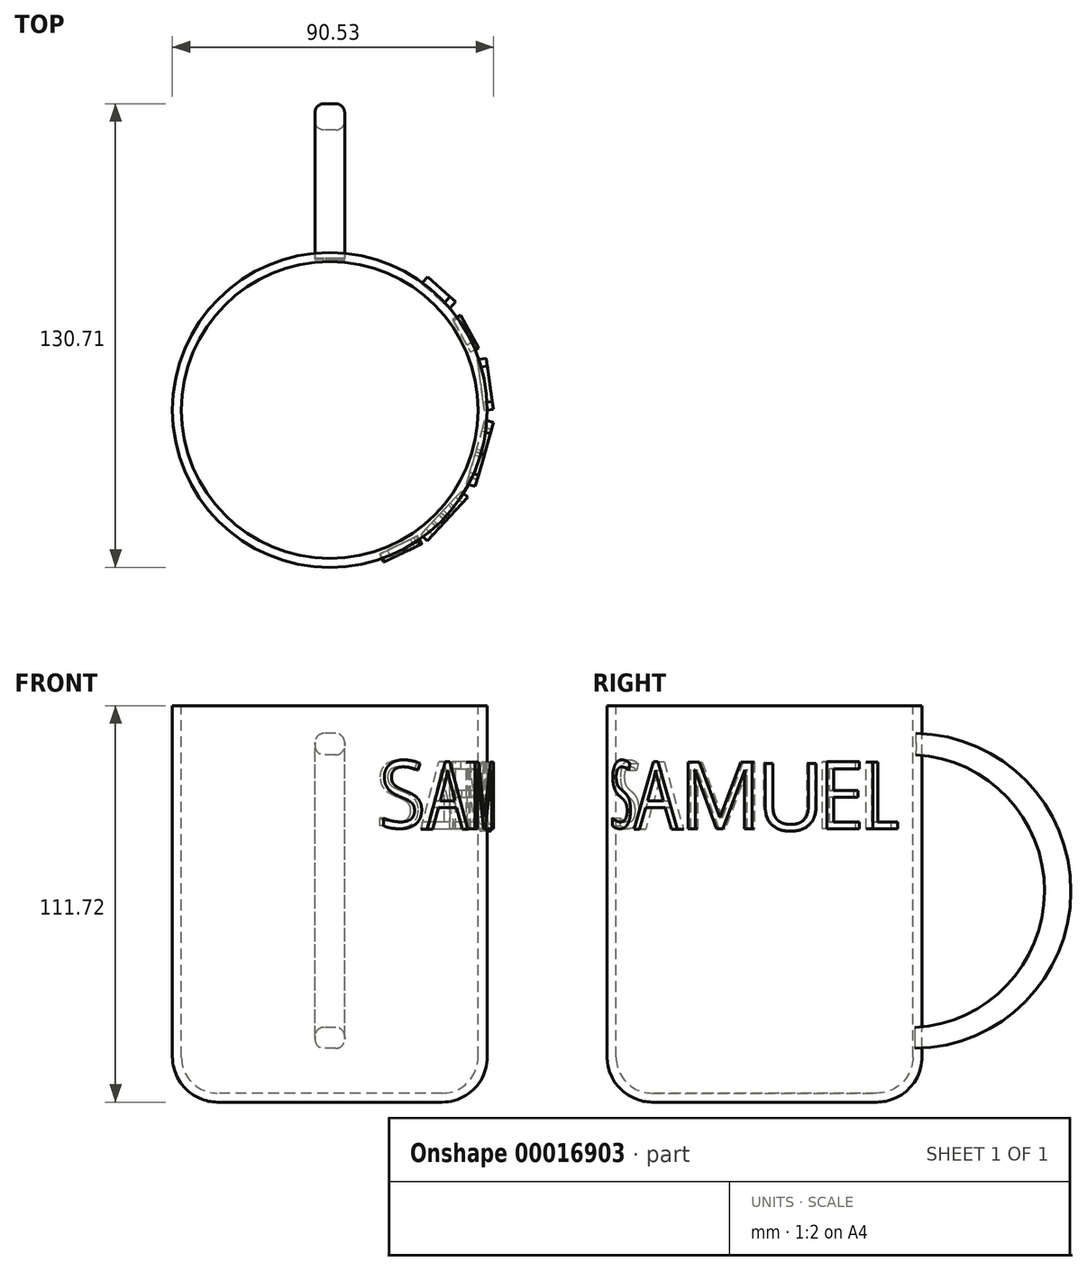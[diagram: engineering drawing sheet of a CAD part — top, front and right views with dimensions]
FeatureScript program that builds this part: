
annotation { "Feature Type Name" : "Feature", "Feature Type Description" : "" }
export const myFeature = defineFeature(function(context is Context, id is Id, definition is map)
    precondition{}
    {
        {
            var Q0;
            Q0=qCreatedBy(makeId("Front.planeOp"),FACE);
            var sketch = newSketch(context, id + "F0", { "sketchPlane" : qUnion([Q0])});
            skLineSegment(sketch, "E0.bottom", {"start": v(0, 46.6) * mm, "end": v(44.36, 46.6) * mm});
            skLineSegment(sketch, "E0.top", {"start": v(0, -65.12) * mm, "end": v(44.36, -65.12) * mm});
            skLineSegment(sketch, "E0.left", {"start": v(0, 46.6) * mm, "end": v(0, -65.12) * mm});
            skLineSegment(sketch, "E0.right", {"start": v(44.36, 46.6) * mm, "end": v(44.36, -65.12) * mm});
            skSolve(sketch);
        }
        {
            var Q0;
            Q0=makeQuery(id+"F0.imprint","IMPRINT",FACE,{"disambiguationData":[TD([[makeQuery(id+"F0.imprint","IMPRINT",EDGE,{"derivedFrom":sQuery(id+"F0.wireOp",EDGE,"E0.bottom")}),-1.0]])]});
            var Q1;
            Q1=sQuery(id+"F0.wireOp",EDGE,"E0.left");
            revolve(context, id + "F1", {"entities" : qUnion([Q0]), "axis" : qUnion([Q1]), "revolveType" : RevolveType.FULL});
        }
        {
            var Q0;
            Q0=makeQuery(id+"F1.opRevolve","SWEPT_EDGE",EDGE,{"disambiguationData":[OSD([sQuery(id+"F0.wireOp",EDGE,"E0.top"),sQuery(id+"F0.wireOp",EDGE,"E0.right")])]});
            fillet(context, id + "F2", {"entities" : qUnion([Q0]), "radius" : 12.7 * mm, "tangentPropagation" : true, "allowEdgeOverflow" : false});
        }
        {
            var Q0;
            Q0=makeQuery(id+"F1.opRevolve","SWEPT_FACE",FACE,{"disambiguationData":[OSD([sQuery(id+"F0.wireOp",EDGE,"E0.bottom")])]});
            shell(context, id + "F3", {"entities" : qUnion([Q0]), "thickness" : 2.54 * mm});
        }
        {
            var Q0;
            Q0=qCreatedBy(makeId("Right.planeOp"),FACE);
            var sketch = newSketch(context, id + "F4", { "sketchPlane" : qUnion([Q0])});
            skText(sketch, "E1", { "text": "S", "fontName": "OpenSans-Regular.ttf"});
            const initialGuessF4  = {"E1": [-0.0061, 0.0296, 1, 0, 0.01905]};
            skSetInitialGuess(sketch, initialGuessF4);
            skSolve(sketch);
        }
        {
            var Q0;
            Q0=makeQuery(id+"F4.imprint","IMPRINT",FACE,{"disambiguationData":[TD([[makeQuery(id+"F4.imprint","IMPRINT",EDGE,{"derivedFrom":sQuery(id+"F4.wireOp",EDGE,"E1.sketch_text.stroke-0")}),-1.0]])]});
            extrude(context, id + "F5", {"entities" : qUnion([Q0]), "depth" : 2.54 * mm});
        }
        {
            var Q0;
            Q0=makeQuery(id+"F5.opExtrude","SWEPT_BODY",BODY,{"disambiguationData":[OSD([sQuery(id+"F4.wireOp",EDGE,"E1.sketch_text.stroke-0"),sQuery(id+"F4.wireOp",EDGE,"E1.sketch_text.stroke-1"),sQuery(id+"F4.wireOp",EDGE,"E1.sketch_text.stroke-2"),sQuery(id+"F4.wireOp",EDGE,"E1.sketch_text.stroke-3"),sQuery(id+"F4.wireOp",EDGE,"E1.sketch_text.stroke-4"),sQuery(id+"F4.wireOp",EDGE,"E1.sketch_text.stroke-5"),sQuery(id+"F4.wireOp",EDGE,"E1.sketch_text.stroke-6"),sQuery(id+"F4.wireOp",EDGE,"E1.sketch_text.stroke-7"),sQuery(id+"F4.wireOp",EDGE,"E1.sketch_text.stroke-8"),sQuery(id+"F4.wireOp",EDGE,"E1.sketch_text.stroke-9"),sQuery(id+"F4.wireOp",EDGE,"E1.sketch_text.stroke-10"),sQuery(id+"F4.wireOp",EDGE,"E1.sketch_text.stroke-11"),sQuery(id+"F4.wireOp",EDGE,"E1.sketch_text.stroke-12"),sQuery(id+"F4.wireOp",EDGE,"E1.sketch_text.stroke-13"),sQuery(id+"F4.wireOp",EDGE,"E1.sketch_text.stroke-14"),sQuery(id+"F4.wireOp",EDGE,"E1.sketch_text.stroke-15"),sQuery(id+"F4.wireOp",EDGE,"E1.sketch_text.stroke-16"),sQuery(id+"F4.wireOp",EDGE,"E1.sketch_text.stroke-17"),sQuery(id+"F4.wireOp",EDGE,"E1.sketch_text.stroke-18"),sQuery(id+"F4.wireOp",EDGE,"E1.sketch_text.stroke-19"),sQuery(id+"F4.wireOp",EDGE,"E1.sketch_text.stroke-20"),sQuery(id+"F4.wireOp",EDGE,"E1.sketch_text.stroke-21"),sQuery(id+"F4.wireOp",EDGE,"E1.sketch_text.stroke-22"),sQuery(id+"F4.wireOp",EDGE,"E1.sketch_text.stroke-23"),sQuery(id+"F4.wireOp",EDGE,"E1.sketch_text.stroke-24")])]});
            transform(context, id + "F6", {"entities" : qUnion([Q0]), "transformType" : TransformType.TRANSLATION_3D, "dx" : 42.69 * mm, "dy" : 0 * mm, "dz" : -17.4 * mm, "makeCopy" : false});
        }
        {
            var Q0;
            Q0=makeQuery(id+"F5.opExtrude","SWEPT_BODY",BODY,{"disambiguationData":[OSD([sQuery(id+"F4.wireOp",EDGE,"E1.sketch_text.stroke-0"),sQuery(id+"F4.wireOp",EDGE,"E1.sketch_text.stroke-1"),sQuery(id+"F4.wireOp",EDGE,"E1.sketch_text.stroke-2"),sQuery(id+"F4.wireOp",EDGE,"E1.sketch_text.stroke-3"),sQuery(id+"F4.wireOp",EDGE,"E1.sketch_text.stroke-4"),sQuery(id+"F4.wireOp",EDGE,"E1.sketch_text.stroke-5"),sQuery(id+"F4.wireOp",EDGE,"E1.sketch_text.stroke-6"),sQuery(id+"F4.wireOp",EDGE,"E1.sketch_text.stroke-7"),sQuery(id+"F4.wireOp",EDGE,"E1.sketch_text.stroke-8"),sQuery(id+"F4.wireOp",EDGE,"E1.sketch_text.stroke-9"),sQuery(id+"F4.wireOp",EDGE,"E1.sketch_text.stroke-10"),sQuery(id+"F4.wireOp",EDGE,"E1.sketch_text.stroke-11"),sQuery(id+"F4.wireOp",EDGE,"E1.sketch_text.stroke-12"),sQuery(id+"F4.wireOp",EDGE,"E1.sketch_text.stroke-13"),sQuery(id+"F4.wireOp",EDGE,"E1.sketch_text.stroke-14"),sQuery(id+"F4.wireOp",EDGE,"E1.sketch_text.stroke-15"),sQuery(id+"F4.wireOp",EDGE,"E1.sketch_text.stroke-16"),sQuery(id+"F4.wireOp",EDGE,"E1.sketch_text.stroke-17"),sQuery(id+"F4.wireOp",EDGE,"E1.sketch_text.stroke-18"),sQuery(id+"F4.wireOp",EDGE,"E1.sketch_text.stroke-19"),sQuery(id+"F4.wireOp",EDGE,"E1.sketch_text.stroke-20"),sQuery(id+"F4.wireOp",EDGE,"E1.sketch_text.stroke-21"),sQuery(id+"F4.wireOp",EDGE,"E1.sketch_text.stroke-22"),sQuery(id+"F4.wireOp",EDGE,"E1.sketch_text.stroke-23"),sQuery(id+"F4.wireOp",EDGE,"E1.sketch_text.stroke-24")])]});
            var Q1;
            Q1=makeQuery(id+"F1.opRevolve","SWEPT_FACE",FACE,{"disambiguationData":[OSD([sQuery(id+"F0.wireOp",EDGE,"E0.right")])]});
            transform(context, id + "F7", {"entities" : qUnion([Q0]), "transformType" : TransformType.ROTATION, "transformAxis" : qUnion([Q1]), "angle" : 64.55 * degree, "oppositeDirection" : true, "makeCopy" : false});
        }
        {
            var Q0;
            Q0=qCreatedBy(makeId("Right.planeOp"),FACE);
            var sketch = newSketch(context, id + "F8", { "sketchPlane" : qUnion([Q0])});
            skText(sketch, "E2", { "text": "A", "fontName": "OpenSans-Regular.ttf"});
            const initialGuessF8  = {"E2": [-0.00816, 0.01185, 1, 0, 0.01905]};
            skSetInitialGuess(sketch, initialGuessF8);
            skSolve(sketch);
        }
        {
            var Q0;
            Q0=makeQuery(id+"F8.imprint","IMPRINT",FACE,{"disambiguationData":[TD([[makeQuery(id+"F8.imprint","IMPRINT",EDGE,{"derivedFrom":sQuery(id+"F8.wireOp",EDGE,"E2.sketch_text.stroke-0")}),-1.0]])]});
            extrude(context, id + "F9", {"entities" : qUnion([Q0]), "depth" : 2.54 * mm});
        }
        {
            var Q0;
            Q0=makeQuery(id+"F9.opExtrude","SWEPT_BODY",BODY,{"disambiguationData":[OSD([sQuery(id+"F8.wireOp",EDGE,"E2.sketch_text.stroke-0"),sQuery(id+"F8.wireOp",EDGE,"E2.sketch_text.stroke-1"),sQuery(id+"F8.wireOp",EDGE,"E2.sketch_text.stroke-2"),sQuery(id+"F8.wireOp",EDGE,"E2.sketch_text.stroke-3"),sQuery(id+"F8.wireOp",EDGE,"E2.sketch_text.stroke-4"),sQuery(id+"F8.wireOp",EDGE,"E2.sketch_text.stroke-5"),sQuery(id+"F8.wireOp",EDGE,"E2.sketch_text.stroke-6"),sQuery(id+"F8.wireOp",EDGE,"E2.sketch_text.stroke-7"),sQuery(id+"F8.wireOp",EDGE,"E2.sketch_text.stroke-8"),sQuery(id+"F8.wireOp",EDGE,"E2.sketch_text.stroke-9"),sQuery(id+"F8.wireOp",EDGE,"E2.sketch_text.stroke-10"),sQuery(id+"F8.wireOp",EDGE,"E2.sketch_text.stroke-11"),sQuery(id+"F8.wireOp",EDGE,"E2.sketch_text.stroke-12")])]});
            transform(context, id + "F10", {"entities" : qUnion([Q0]), "transformType" : TransformType.TRANSLATION_3D, "dx" : 42.68 * mm, "dy" : 0 * mm, "dz" : 0 * mm, "makeCopy" : false});
        }
        {
            var Q0;
            Q0=makeQuery(id+"F9.opExtrude","SWEPT_BODY",BODY,{"disambiguationData":[OSD([sQuery(id+"F8.wireOp",EDGE,"E2.sketch_text.stroke-0"),sQuery(id+"F8.wireOp",EDGE,"E2.sketch_text.stroke-1"),sQuery(id+"F8.wireOp",EDGE,"E2.sketch_text.stroke-2"),sQuery(id+"F8.wireOp",EDGE,"E2.sketch_text.stroke-3"),sQuery(id+"F8.wireOp",EDGE,"E2.sketch_text.stroke-4"),sQuery(id+"F8.wireOp",EDGE,"E2.sketch_text.stroke-5"),sQuery(id+"F8.wireOp",EDGE,"E2.sketch_text.stroke-6"),sQuery(id+"F8.wireOp",EDGE,"E2.sketch_text.stroke-7"),sQuery(id+"F8.wireOp",EDGE,"E2.sketch_text.stroke-8"),sQuery(id+"F8.wireOp",EDGE,"E2.sketch_text.stroke-9"),sQuery(id+"F8.wireOp",EDGE,"E2.sketch_text.stroke-10"),sQuery(id+"F8.wireOp",EDGE,"E2.sketch_text.stroke-11"),sQuery(id+"F8.wireOp",EDGE,"E2.sketch_text.stroke-12")])]});
            var Q1;
            Q1=makeQuery(id+"F1.opRevolve","SWEPT_FACE",FACE,{"disambiguationData":[OSD([sQuery(id+"F0.wireOp",EDGE,"E0.right")])]});
            transform(context, id + "F11", {"entities" : qUnion([Q0]), "transformType" : TransformType.ROTATION, "transformAxis" : qUnion([Q1]), "angle" : 43.05 * degree, "oppositeDirection" : true, "makeCopy" : false});
        }
        {
            var Q0;
            Q0=qCreatedBy(makeId("Right.planeOp"),FACE);
            var sketch = newSketch(context, id + "F12", { "sketchPlane" : qUnion([Q0])});
            skText(sketch, "E3", { "text": "M", "fontName": "OpenSans-Regular.ttf"});
            const initialGuessF12  = {"E3": [-0.00669, 0.01221, 1, 0, 0.01905]};
            skSetInitialGuess(sketch, initialGuessF12);
            skSolve(sketch);
        }
        {
            var Q0;
            Q0=makeQuery(id+"F12.imprint","IMPRINT",FACE,{"disambiguationData":[TD([[makeQuery(id+"F12.imprint","IMPRINT",EDGE,{"derivedFrom":sQuery(id+"F12.wireOp",EDGE,"E3.sketch_text.stroke-0")}),-1.0]])]});
            extrude(context, id + "F13", {"entities" : qUnion([Q0]), "depth" : 2.54 * mm});
        }
        {
            var Q0;
            Q0=makeQuery(id+"F13.opExtrude","SWEPT_BODY",BODY,{"disambiguationData":[OSD([sQuery(id+"F12.wireOp",EDGE,"E3.sketch_text.stroke-0"),sQuery(id+"F12.wireOp",EDGE,"E3.sketch_text.stroke-1"),sQuery(id+"F12.wireOp",EDGE,"E3.sketch_text.stroke-2"),sQuery(id+"F12.wireOp",EDGE,"E3.sketch_text.stroke-3"),sQuery(id+"F12.wireOp",EDGE,"E3.sketch_text.stroke-4"),sQuery(id+"F12.wireOp",EDGE,"E3.sketch_text.stroke-5"),sQuery(id+"F12.wireOp",EDGE,"E3.sketch_text.stroke-6"),sQuery(id+"F12.wireOp",EDGE,"E3.sketch_text.stroke-7"),sQuery(id+"F12.wireOp",EDGE,"E3.sketch_text.stroke-8"),sQuery(id+"F12.wireOp",EDGE,"E3.sketch_text.stroke-9"),sQuery(id+"F12.wireOp",EDGE,"E3.sketch_text.stroke-10"),sQuery(id+"F12.wireOp",EDGE,"E3.sketch_text.stroke-11"),sQuery(id+"F12.wireOp",EDGE,"E3.sketch_text.stroke-12"),sQuery(id+"F12.wireOp",EDGE,"E3.sketch_text.stroke-13"),sQuery(id+"F12.wireOp",EDGE,"E3.sketch_text.stroke-14"),sQuery(id+"F12.wireOp",EDGE,"E3.sketch_text.stroke-15"),sQuery(id+"F12.wireOp",EDGE,"E3.sketch_text.stroke-16"),sQuery(id+"F12.wireOp",EDGE,"E3.sketch_text.stroke-17")])]});
            transform(context, id + "F14", {"entities" : qUnion([Q0]), "transformType" : TransformType.TRANSLATION_3D, "dx" : 42.8 * mm, "dy" : -5.2 * mm, "dz" : -0.34 * mm, "makeCopy" : false});
        }
        {
            var Q0;
            Q0=qCreatedBy(makeId("Right.planeOp"),FACE);
            var sketch = newSketch(context, id + "F15", { "sketchPlane" : qUnion([Q0])});
            skText(sketch, "E4", { "text": "U", "fontName": "OpenSans-Regular.ttf"});
            const initialGuessF15  = {"E4": [-0.0073, 0.0122, 1, 0, 0.01905]};
            skSetInitialGuess(sketch, initialGuessF15);
            skSolve(sketch);
        }
        {
            var Q0;
            Q0=makeQuery(id+"F15.imprint","IMPRINT",FACE,{"disambiguationData":[TD([[makeQuery(id+"F15.imprint","IMPRINT",EDGE,{"derivedFrom":sQuery(id+"F15.wireOp",EDGE,"E4.sketch_text.stroke-0")}),-1.0]])]});
            extrude(context, id + "F16", {"entities" : qUnion([Q0]), "depth" : 2.54 * mm});
        }
        {
            var Q0;
            Q0=makeQuery(id+"F16.opExtrude","SWEPT_BODY",BODY,{"disambiguationData":[OSD([sQuery(id+"F15.wireOp",EDGE,"E4.sketch_text.stroke-0"),sQuery(id+"F15.wireOp",EDGE,"E4.sketch_text.stroke-1"),sQuery(id+"F15.wireOp",EDGE,"E4.sketch_text.stroke-2"),sQuery(id+"F15.wireOp",EDGE,"E4.sketch_text.stroke-3"),sQuery(id+"F15.wireOp",EDGE,"E4.sketch_text.stroke-4"),sQuery(id+"F15.wireOp",EDGE,"E4.sketch_text.stroke-5"),sQuery(id+"F15.wireOp",EDGE,"E4.sketch_text.stroke-6"),sQuery(id+"F15.wireOp",EDGE,"E4.sketch_text.stroke-7"),sQuery(id+"F15.wireOp",EDGE,"E4.sketch_text.stroke-8"),sQuery(id+"F15.wireOp",EDGE,"E4.sketch_text.stroke-9"),sQuery(id+"F15.wireOp",EDGE,"E4.sketch_text.stroke-10"),sQuery(id+"F15.wireOp",EDGE,"E4.sketch_text.stroke-11"),sQuery(id+"F15.wireOp",EDGE,"E4.sketch_text.stroke-12"),sQuery(id+"F15.wireOp",EDGE,"E4.sketch_text.stroke-13")])]});
            transform(context, id + "F17", {"entities" : qUnion([Q0]), "transformType" : TransformType.TRANSLATION_3D, "dx" : 43.14 * mm, "dy" : -1.16 * mm, "dz" : -0.71 * mm, "makeCopy" : false});
        }
        {
            var Q0;
            Q0=makeQuery(id+"F16.opExtrude","SWEPT_BODY",BODY,{"disambiguationData":[OSD([sQuery(id+"F15.wireOp",EDGE,"E4.sketch_text.stroke-0"),sQuery(id+"F15.wireOp",EDGE,"E4.sketch_text.stroke-1"),sQuery(id+"F15.wireOp",EDGE,"E4.sketch_text.stroke-2"),sQuery(id+"F15.wireOp",EDGE,"E4.sketch_text.stroke-3"),sQuery(id+"F15.wireOp",EDGE,"E4.sketch_text.stroke-4"),sQuery(id+"F15.wireOp",EDGE,"E4.sketch_text.stroke-5"),sQuery(id+"F15.wireOp",EDGE,"E4.sketch_text.stroke-6"),sQuery(id+"F15.wireOp",EDGE,"E4.sketch_text.stroke-7"),sQuery(id+"F15.wireOp",EDGE,"E4.sketch_text.stroke-8"),sQuery(id+"F15.wireOp",EDGE,"E4.sketch_text.stroke-9"),sQuery(id+"F15.wireOp",EDGE,"E4.sketch_text.stroke-10"),sQuery(id+"F15.wireOp",EDGE,"E4.sketch_text.stroke-11"),sQuery(id+"F15.wireOp",EDGE,"E4.sketch_text.stroke-12"),sQuery(id+"F15.wireOp",EDGE,"E4.sketch_text.stroke-13")])]});
            var Q1;
            Q1=makeQuery(id+"F1.opRevolve","SWEPT_FACE",FACE,{"disambiguationData":[OSD([sQuery(id+"F0.wireOp",EDGE,"E0.right")])]});
            transform(context, id + "F18", {"entities" : qUnion([Q0]), "transformType" : TransformType.ROTATION, "transformAxis" : qUnion([Q1]), "angle" : 7.82 * degree, "makeCopy" : false});
        }
        {
            var Q0;
            Q0=qCreatedBy(makeId("Right.planeOp"),FACE);
            var sketch = newSketch(context, id + "F19", { "sketchPlane" : qUnion([Q0])});
            skText(sketch, "E5", { "text": "E", "fontName": "OpenSans-Regular.ttf"});
            const initialGuessF19  = {"E5": [-0.00748, 0.01207, 1, 0, 0.01905]};
            skSetInitialGuess(sketch, initialGuessF19);
            skSolve(sketch);
        }
        {
            var Q0;
            Q0=makeQuery(id+"F19.imprint","IMPRINT",FACE,{"disambiguationData":[TD([[makeQuery(id+"F19.imprint","IMPRINT",EDGE,{"derivedFrom":sQuery(id+"F19.wireOp",EDGE,"E5.sketch_text.stroke-0")}),-1.0]])]});
            extrude(context, id + "F20", {"entities" : qUnion([Q0]), "depth" : 2.54 * mm});
        }
        {
            var Q0;
            Q0=makeQuery(id+"F20.opExtrude","SWEPT_BODY",BODY,{"disambiguationData":[OSD([sQuery(id+"F19.wireOp",EDGE,"E5.sketch_text.stroke-0"),sQuery(id+"F19.wireOp",EDGE,"E5.sketch_text.stroke-1"),sQuery(id+"F19.wireOp",EDGE,"E5.sketch_text.stroke-2"),sQuery(id+"F19.wireOp",EDGE,"E5.sketch_text.stroke-3"),sQuery(id+"F19.wireOp",EDGE,"E5.sketch_text.stroke-4"),sQuery(id+"F19.wireOp",EDGE,"E5.sketch_text.stroke-5"),sQuery(id+"F19.wireOp",EDGE,"E5.sketch_text.stroke-6"),sQuery(id+"F19.wireOp",EDGE,"E5.sketch_text.stroke-7"),sQuery(id+"F19.wireOp",EDGE,"E5.sketch_text.stroke-8"),sQuery(id+"F19.wireOp",EDGE,"E5.sketch_text.stroke-9"),sQuery(id+"F19.wireOp",EDGE,"E5.sketch_text.stroke-10"),sQuery(id+"F19.wireOp",EDGE,"E5.sketch_text.stroke-11")])]});
            transform(context, id + "F21", {"entities" : qUnion([Q0]), "transformType" : TransformType.TRANSLATION_3D, "dx" : 42.63 * mm, "dy" : 0 * mm, "dz" : -0.18 * mm, "makeCopy" : false});
        }
        {
            var Q0;
            Q0=makeQuery(id+"F20.opExtrude","SWEPT_BODY",BODY,{"disambiguationData":[OSD([sQuery(id+"F19.wireOp",EDGE,"E5.sketch_text.stroke-0"),sQuery(id+"F19.wireOp",EDGE,"E5.sketch_text.stroke-1"),sQuery(id+"F19.wireOp",EDGE,"E5.sketch_text.stroke-2"),sQuery(id+"F19.wireOp",EDGE,"E5.sketch_text.stroke-3"),sQuery(id+"F19.wireOp",EDGE,"E5.sketch_text.stroke-4"),sQuery(id+"F19.wireOp",EDGE,"E5.sketch_text.stroke-5"),sQuery(id+"F19.wireOp",EDGE,"E5.sketch_text.stroke-6"),sQuery(id+"F19.wireOp",EDGE,"E5.sketch_text.stroke-7"),sQuery(id+"F19.wireOp",EDGE,"E5.sketch_text.stroke-8"),sQuery(id+"F19.wireOp",EDGE,"E5.sketch_text.stroke-9"),sQuery(id+"F19.wireOp",EDGE,"E5.sketch_text.stroke-10"),sQuery(id+"F19.wireOp",EDGE,"E5.sketch_text.stroke-11")])]});
            var Q1;
            Q1=makeQuery(id+"F1.opRevolve","SWEPT_FACE",FACE,{"disambiguationData":[OSD([sQuery(id+"F0.wireOp",EDGE,"E0.right")])]});
            transform(context, id + "F22", {"entities" : qUnion([Q0]), "transformType" : TransformType.ROTATION, "transformAxis" : qUnion([Q1]), "angle" : 28.87 * degree, "makeCopy" : false});
        }
        {
            var Q0;
            Q0=makeQuery(id+"F13.opExtrude","SWEPT_BODY",BODY,{"disambiguationData":[OSD([sQuery(id+"F12.wireOp",EDGE,"E3.sketch_text.stroke-0"),sQuery(id+"F12.wireOp",EDGE,"E3.sketch_text.stroke-1"),sQuery(id+"F12.wireOp",EDGE,"E3.sketch_text.stroke-2"),sQuery(id+"F12.wireOp",EDGE,"E3.sketch_text.stroke-3"),sQuery(id+"F12.wireOp",EDGE,"E3.sketch_text.stroke-4"),sQuery(id+"F12.wireOp",EDGE,"E3.sketch_text.stroke-5"),sQuery(id+"F12.wireOp",EDGE,"E3.sketch_text.stroke-6"),sQuery(id+"F12.wireOp",EDGE,"E3.sketch_text.stroke-7"),sQuery(id+"F12.wireOp",EDGE,"E3.sketch_text.stroke-8"),sQuery(id+"F12.wireOp",EDGE,"E3.sketch_text.stroke-9"),sQuery(id+"F12.wireOp",EDGE,"E3.sketch_text.stroke-10"),sQuery(id+"F12.wireOp",EDGE,"E3.sketch_text.stroke-11"),sQuery(id+"F12.wireOp",EDGE,"E3.sketch_text.stroke-12"),sQuery(id+"F12.wireOp",EDGE,"E3.sketch_text.stroke-13"),sQuery(id+"F12.wireOp",EDGE,"E3.sketch_text.stroke-14"),sQuery(id+"F12.wireOp",EDGE,"E3.sketch_text.stroke-15"),sQuery(id+"F12.wireOp",EDGE,"E3.sketch_text.stroke-16"),sQuery(id+"F12.wireOp",EDGE,"E3.sketch_text.stroke-17")])]});
            var Q1;
            Q1=makeQuery(id+"F1.opRevolve","SWEPT_FACE",FACE,{"disambiguationData":[OSD([sQuery(id+"F0.wireOp",EDGE,"E0.right")])]});
            transform(context, id + "F23", {"entities" : qUnion([Q0]), "transformType" : TransformType.ROTATION, "transformAxis" : qUnion([Q1]), "angle" : 16.12 * degree, "oppositeDirection" : true, "makeCopy" : false});
        }
        {
            var Q0;
            Q0=qCreatedBy(makeId("Right.planeOp"),FACE);
            var sketch = newSketch(context, id + "F24", { "sketchPlane" : qUnion([Q0])});
            skText(sketch, "E6", { "text": "L", "fontName": "OpenSans-Regular.ttf"});
            const initialGuessF24  = {"E6": [-0.00865, 0.01265, 1, 0, 0.01905]};
            skSetInitialGuess(sketch, initialGuessF24);
            skSolve(sketch);
        }
        {
            var Q0;
            Q0=makeQuery(id+"F24.imprint","IMPRINT",FACE,{"disambiguationData":[TD([[makeQuery(id+"F24.imprint","IMPRINT",EDGE,{"derivedFrom":sQuery(id+"F24.wireOp",EDGE,"E6.sketch_text.stroke-0")}),-1.0]])]});
            extrude(context, id + "F25", {"entities" : qUnion([Q0]), "depth" : 2.54 * mm});
        }
        {
            var Q0;
            Q0=makeQuery(id+"F25.opExtrude","SWEPT_BODY",BODY,{"disambiguationData":[OSD([sQuery(id+"F24.wireOp",EDGE,"E6.sketch_text.stroke-0"),sQuery(id+"F24.wireOp",EDGE,"E6.sketch_text.stroke-1"),sQuery(id+"F24.wireOp",EDGE,"E6.sketch_text.stroke-2"),sQuery(id+"F24.wireOp",EDGE,"E6.sketch_text.stroke-3"),sQuery(id+"F24.wireOp",EDGE,"E6.sketch_text.stroke-4"),sQuery(id+"F24.wireOp",EDGE,"E6.sketch_text.stroke-5")])]});
            transform(context, id + "F26", {"entities" : qUnion([Q0]), "transformType" : TransformType.TRANSLATION_3D, "dx" : 43.87 * mm, "dy" : 0 * mm, "dz" : -0.78 * mm, "makeCopy" : false});
        }
        {
            var Q0;
            Q0=makeQuery(id+"F25.opExtrude","SWEPT_BODY",BODY,{"disambiguationData":[OSD([sQuery(id+"F24.wireOp",EDGE,"E6.sketch_text.stroke-0"),sQuery(id+"F24.wireOp",EDGE,"E6.sketch_text.stroke-1"),sQuery(id+"F24.wireOp",EDGE,"E6.sketch_text.stroke-2"),sQuery(id+"F24.wireOp",EDGE,"E6.sketch_text.stroke-3"),sQuery(id+"F24.wireOp",EDGE,"E6.sketch_text.stroke-4"),sQuery(id+"F24.wireOp",EDGE,"E6.sketch_text.stroke-5")])]});
            var Q1;
            Q1=makeQuery(id+"F1.opRevolve","SWEPT_FACE",FACE,{"disambiguationData":[OSD([sQuery(id+"F0.wireOp",EDGE,"E0.right")])]});
            transform(context, id + "F27", {"entities" : qUnion([Q0]), "transformType" : TransformType.ROTATION, "transformAxis" : qUnion([Q1]), "angle" : 48.14 * degree, "makeCopy" : false});
        }
        {
            var Q0;
            Q0=qCreatedBy(makeId("Right.planeOp"),FACE);
            var sketch = newSketch(context, id + "F28", { "sketchPlane" : qUnion([Q0])});
            skArc(sketch, "E7", {"start": v(44.11, -44.05) * mm, "mid": v(80.64, -5.75) * mm, "end": v(44.36, 32.78) * mm});
            skArc(sketch, "E8", {"start": v(44.11, -49.96) * mm, "mid": v(88.06, -5.76) * mm, "end": v(44.49, 38.81) * mm});
            skLineSegment(sketch, "E9", {"start": v(44.49, 38.81) * mm, "end": v(44.36, 32.78) * mm});
            skLineSegment(sketch, "E10", {"start": v(44.11, -44.05) * mm, "end": v(44.11, -49.96) * mm});
            skSolve(sketch);
        }
        {
            var Q0;
            Q0=makeQuery(id+"F28.imprint","IMPRINT",FACE,{"disambiguationData":[TD([[makeQuery(id+"F28.imprint","IMPRINT",EDGE,{"derivedFrom":sQuery(id+"F28.wireOp",EDGE,"E7")}),-1.0]])]});
            extrude(context, id + "F29", {"entities" : qUnion([Q0]), "depth" : 8.35 * mm});
        }
        {
            var Q0;
            Q0=makeQuery(id+"F29.opExtrude","SWEPT_BODY",BODY,{"disambiguationData":[OSD([sQuery(id+"F28.wireOp",EDGE,"E7"),sQuery(id+"F28.wireOp",EDGE,"E8"),sQuery(id+"F28.wireOp",EDGE,"E9"),sQuery(id+"F28.wireOp",EDGE,"E10")])]});
            transform(context, id + "F30", {"entities" : qUnion([Q0]), "transformType" : TransformType.TRANSLATION_3D, "dx" : -4.18 * mm, "dy" : -1.71 * mm, "dz" : 0 * mm, "makeCopy" : false});
        }
        {
            var Q0;
            Q0=makeQuery(id+"F29.opExtrude","CAP_EDGE",EDGE,{"disambiguationData":[OSD([sQuery(id+"F28.wireOp",EDGE,"E7")])],"isStart":false});
            var Q1;
            Q1=makeQuery(id+"F29.opExtrude","CAP_EDGE",EDGE,{"disambiguationData":[OSD([sQuery(id+"F28.wireOp",EDGE,"E8")])],"isStart":false});
            var Q2;
            Q2=makeQuery(id+"F29.opExtrude","CAP_EDGE",EDGE,{"disambiguationData":[OSD([sQuery(id+"F28.wireOp",EDGE,"E8")])],"isStart":true});
            var Q3;
            Q3=makeQuery(id+"F29.opExtrude","CAP_EDGE",EDGE,{"disambiguationData":[OSD([sQuery(id+"F28.wireOp",EDGE,"E7")])],"isStart":true});
            fillet(context, id + "F31", {"entities" : qUnion([Q0, Q1, Q2, Q3]), "radius" : 2.54 * mm, "tangentPropagation" : true, "allowEdgeOverflow" : false});
        }
    });
